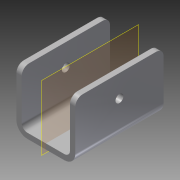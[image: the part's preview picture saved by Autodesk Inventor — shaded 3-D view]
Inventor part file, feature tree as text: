
AUTODESK INVENTOR PART (.ipt)
format: ipt  version: 2013 (Build 170138000, 138)  size: 121,344 bytes
history: native  units: in
note: dims shown in document units (in); Inventor stores cm internally (conversion verified against a paired STEP export)
features: plane x2, sketch x2, extrude x1, fillet x1, hole x1
ambient origin geometry x8: Origin, YZ Plane, XZ Plane, XY Plane, X Axis, Y Axis, Z Axis, Center Point
bodies: Solid1 (feature_tree)
feature tree (7):
  extrude  "Extrusion1"  Depth=2.0in
  fillet  "Fillet1"  Radius=0.18in
  hole  "Hole1"  [1 undecoded]
  plane  "Work Plane1"
  plane  "Work Plane2"
  sketch  "Sketch1"  dims[d0=2.0in d1=2.0in d2=0.18in]
  sketch  "Sketch2"  dims[d3=0.18in d4=0.18in d5=0.19in d6=0.37in d7=3.0in d8=0.0in d9=0.25in d10=1.25in d11=0.27in d12=0.75in d13=0.375in d14=0.25in d15=0.5635in d16=1.0in d17=0.8108in]
note: 1 required parameter value undecoded (feature->parameter linkage not recoverable at this tier; creation-order binding heuristic only, values carry confidence <= 0.55)
